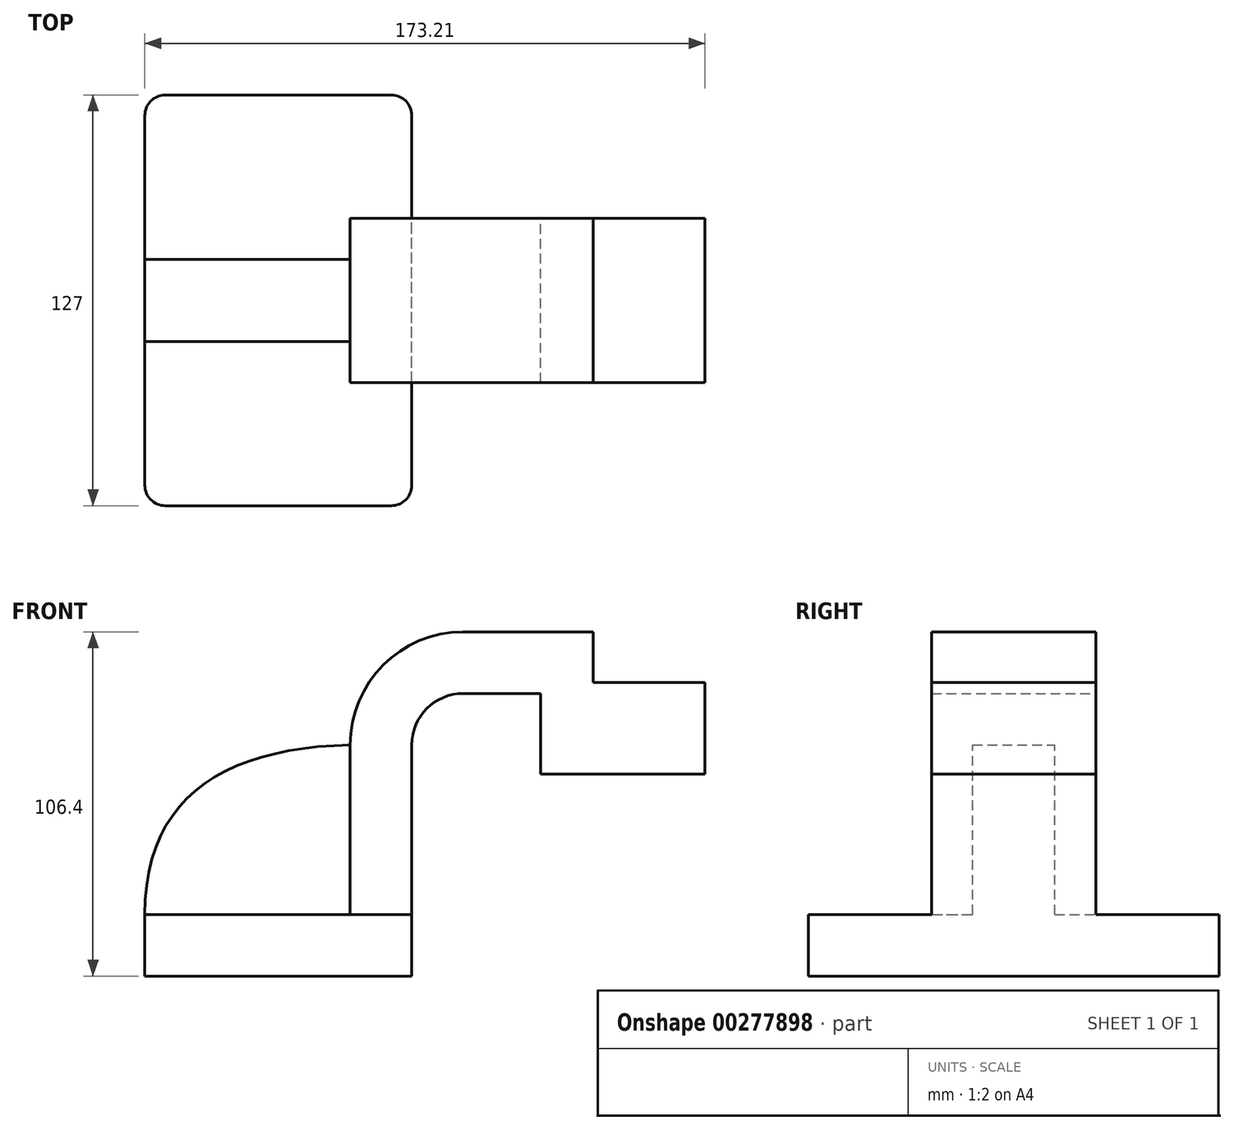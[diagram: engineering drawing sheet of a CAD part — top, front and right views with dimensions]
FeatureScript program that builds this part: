
annotation { "Feature Type Name" : "Feature", "Feature Type Description" : "" }
export const myFeature = defineFeature(function(context is Context, id is Id, definition is map)
    precondition{}
    {
        {
            var Q0;
            Q0=qCreatedBy(makeId("Front.planeOp"),FACE);
            var sketch = newSketch(context, id + "F0", { "sketchPlane" : qUnion([Q0])});
            skLineSegment(sketch, "E0.bottom", {"start": v(41.28, -9.52) * mm, "end": v(-41.27, -9.53) * mm});
            skLineSegment(sketch, "E0.top", {"start": v(41.27, 9.53) * mm, "end": v(-41.28, 9.53) * mm});
            skLineSegment(sketch, "E0.left", {"start": v(41.28, -9.52) * mm, "end": v(41.28, 9.53) * mm});
            skLineSegment(sketch, "E0.right", {"start": v(-41.27, -9.53) * mm, "end": v(-41.28, 9.53) * mm});
            skPoint(sketch, "E0.middle", {"position": v(0, 0) * mm});
            skLineSegment(sketch, "E1.bottom", {"start": v(131.93, 52.93) * mm, "end": v(81.13, 52.93) * mm});
            skLineSegment(sketch, "E1.top", {"start": v(131.93, 81.19) * mm, "end": v(81.13, 81.19) * mm});
            skLineSegment(sketch, "E1.left", {"start": v(131.93, 52.93) * mm, "end": v(131.93, 81.19) * mm});
            skLineSegment(sketch, "E1.right", {"start": v(81.13, 52.93) * mm, "end": v(81.13, 81.19) * mm});
            skPoint(sketch, "E1.middle", {"position": v(106.53, 67.06) * mm});
            skLineSegment(sketch, "E2", {"start": v(41.27, 9.53) * mm, "end": v(41.27, 61.94) * mm});
            skArc(sketch, "E3", {"start": v(41.27, 61.94) * mm, "mid": v(45.92, 73.17) * mm, "end": v(57.15, 77.82) * mm});
            skLineSegment(sketch, "E4", {"start": v(57.15, 77.82) * mm, "end": v(97.35, 77.82) * mm});
            skLineSegment(sketch, "E5.0", {"start": v(57.15, 96.87) * mm, "end": v(97.35, 96.87) * mm});
            skArc(sketch, "E5.1", {"start": v(22.23, 61.94) * mm, "mid": v(32.45, 86.64) * mm, "end": v(57.15, 96.87) * mm});
            skLineSegment(sketch, "E5.2", {"start": v(22.22, 9.53) * mm, "end": v(22.22, 61.94) * mm});
            skLineSegment(sketch, "E6", {"start": v(97.35, 77.82) * mm, "end": v(97.35, 96.87) * mm});
            skFitSpline(sketch, "E7", {"points": [v(-41.28, 9.53) * mm, v(22.23, 61.94) * mm], "startDerivative": vector(0.16, 107.92) * mm, "endDerivative": vector(118.17, 2.93) * mm});
            skSolve(sketch);
        }
        {
            var Q0;
            Q0=makeQuery(id+"F0.imprint","IMPRINT",FACE,{"disambiguationData":[TD([[makeQuery(id+"F0.imprint","IMPRINT",EDGE,{"derivedFrom":sQuery(id+"F0.wireOp",EDGE,"E0.bottom")}),-1.0]])]});
            extrude(context, id + "F1", {"entities" : qUnion([Q0]), "endBound" : BoundingType.SYMMETRIC, "depth" : 127 * mm});
        }
        {
            var Q0;
            {var subQ1=sQuery(id+"F0.wireOp",EDGE,"E1.bottom");Q0=makeQuery(id+"F0.imprint","IMPRINT",FACE,{"disambiguationData":[TD([[makeQuery(id+"F0.imprint","IMPRINT",EDGE,{"derivedFrom":subQ1}),-1.0]])]});}
            var Q1;
            Q1=makeQuery(id+"F0.imprint","IMPRINT",FACE,{"disambiguationData":[TD([[makeQuery(id+"F0.imprint","IMPRINT",EDGE,{"derivedFrom":sQuery(id+"F0.wireOp",EDGE,"E0.bottom")}),-1.0]])]});
            var Q2;
            {var subQ0=sQuery(id+"F0.wireOp",EDGE,"E1.right");var subQ1=sQuery(id+"F0.wireOp",EDGE,"E1.top");var subQ2=makeQuery(id+"F0.imprint","INTERSECT",VERTEX,{"derivedFrom":[subQ1,subQ0]});Q2=makeQuery(id+"F0.imprint","IMPRINT",FACE,{"disambiguationData":[TD([[makeQuery(id+"F0.imprint","IMPRINT",EDGE,{"disambiguationData":[TD([[subQ2,1.0]])],"derivedFrom":subQ1}),1.0]])]});}
            var Q3;
            {var subQ0=sQuery(id+"F0.wireOp",EDGE,"E2");Q3=makeQuery(id+"F0.imprint","IMPRINT",FACE,{"disambiguationData":[TD([[makeQuery(id+"F0.imprint","IMPRINT",EDGE,{"derivedFrom":subQ0}),1.0]])]});}
            extrude(context, id + "F2", {"entities" : qUnion([Q0, Q1, Q2, Q3]), "operationType" : NewBodyOperationType.ADD, "endBound" : BoundingType.SYMMETRIC, "depth" : 50.8 * mm});
        }
        {
            var Q0;
            {var subQ2=sQuery(id+"F0.wireOp",EDGE,"E5.2");Q0=makeQuery(id+"F0.imprint","IMPRINT",FACE,{"disambiguationData":[TD([[makeQuery(id+"F0.imprint","IMPRINT",EDGE,{"derivedFrom":subQ2}),1.0]])]});}
            extrude(context, id + "F3", {"entities" : qUnion([Q0]), "operationType" : NewBodyOperationType.ADD, "endBound" : BoundingType.SYMMETRIC, "depth" : 25.4 * mm});
        }
        {
            var Q0;
            Q0=makeQuery(id+"F1.opExtrude","CAP_EDGE",EDGE,{"disambiguationData":[OSD([sQuery(id+"F0.wireOp",EDGE,"E0.left")])],"isStart":false});
            var Q1;
            Q1=makeQuery(id+"F1.opExtrude","CAP_EDGE",EDGE,{"disambiguationData":[OSD([sQuery(id+"F0.wireOp",EDGE,"E0.right")])],"isStart":false});
            var Q2;
            Q2=makeQuery(id+"F1.opExtrude","CAP_EDGE",EDGE,{"disambiguationData":[OSD([sQuery(id+"F0.wireOp",EDGE,"E0.left")])],"isStart":true});
            var Q3;
            Q3=makeQuery(id+"F1.opExtrude","CAP_EDGE",EDGE,{"disambiguationData":[OSD([sQuery(id+"F0.wireOp",EDGE,"E0.right")])],"isStart":true});
            fillet(context, id + "F4", {"entities" : qUnion([Q0, Q1, Q2, Q3]), "radius" : 6.35 * mm, "tangentPropagation" : true, "allowEdgeOverflow" : false});
        }
    });
